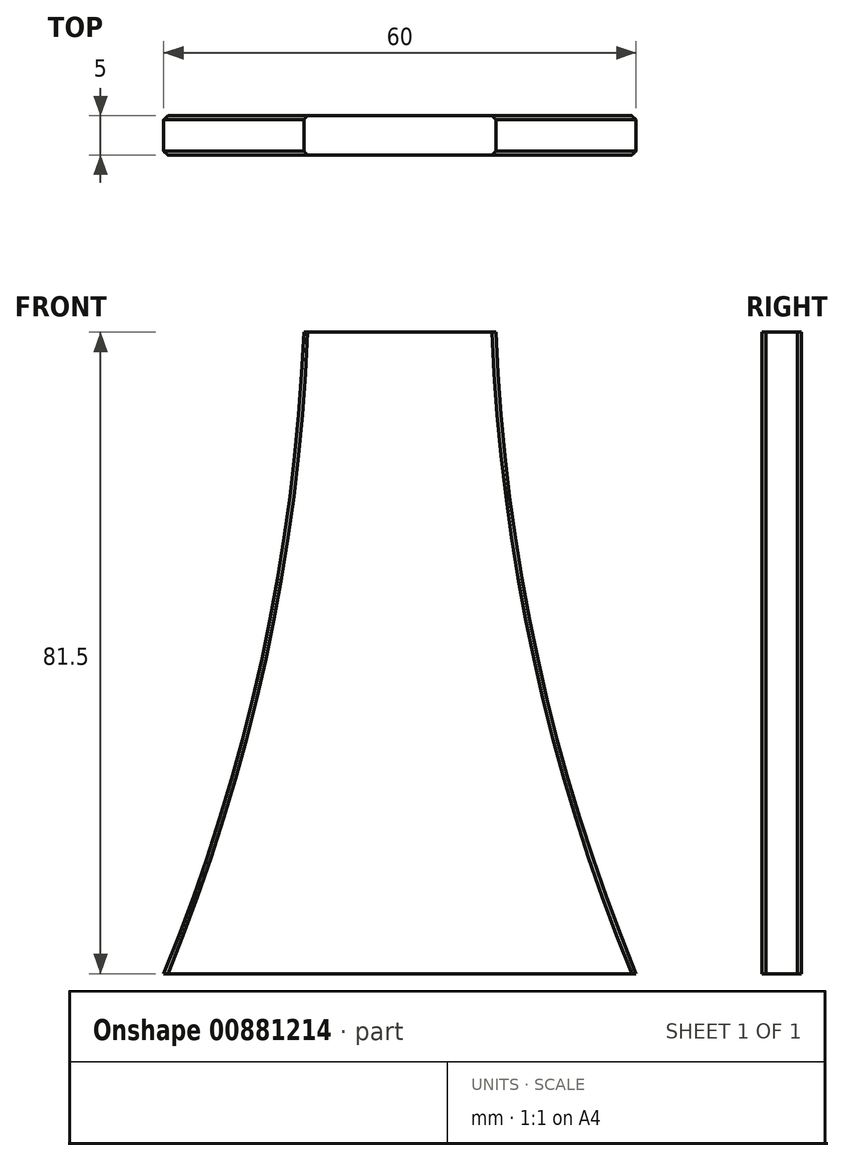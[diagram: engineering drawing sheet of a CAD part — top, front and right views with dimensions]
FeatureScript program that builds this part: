
annotation { "Feature Type Name" : "Feature", "Feature Type Description" : "" }
export const myFeature = defineFeature(function(context is Context, id is Id, definition is map)
    precondition{}
    {
        {
            var Q0;
            Q0=qCreatedBy(makeId("Front.planeOp"),FACE);
            var sketch = newSketch(context, id + "F0", { "sketchPlane" : qUnion([Q0])});
            skLineSegment(sketch, "E0", {"start": v(-12.2, 40.75) * mm, "end": v(12.2, 40.75) * mm});
            skLineSegment(sketch, "E1", {"start": v(-30, -40.75) * mm, "end": v(30, -40.75) * mm});
            skArc(sketch, "E2", {"start": v(-30, -40.75) * mm, "mid": v(-17.53, -0.78) * mm, "end": v(-12.2, 40.75) * mm});
            skArc(sketch, "E3", {"start": v(12.2, 40.75) * mm, "mid": v(17.53, -0.78) * mm, "end": v(30, -40.75) * mm});
            skSolve(sketch);
        }
        {
            var Q0;
            Q0=makeQuery(id+"F0.imprint","IMPRINT",FACE,{"disambiguationData":[TD([[makeQuery(id+"F0.imprint","IMPRINT",EDGE,{"derivedFrom":sQuery(id+"F0.wireOp",EDGE,"E0")}),-1.0]])]});
            extrude(context, id + "F1", {"entities" : qUnion([Q0]), "depth" : 5 * mm, "offsetDistance" : 25 * mm});
        }
        {
            var Q0;
            Q0=makeQuery(id+"F1.opExtrude","CAP_EDGE",EDGE,{"disambiguationData":[OSD([sQuery(id+"F0.wireOp",EDGE,"E2")])],"isStart":true});
            var Q1;
            Q1=makeQuery(id+"F1.opExtrude","CAP_EDGE",EDGE,{"disambiguationData":[OSD([sQuery(id+"F0.wireOp",EDGE,"E2")])],"isStart":false});
            var Q2;
            Q2=makeQuery(id+"F1.opExtrude","CAP_EDGE",EDGE,{"disambiguationData":[OSD([sQuery(id+"F0.wireOp",EDGE,"E3")])],"isStart":false});
            var Q3;
            Q3=makeQuery(id+"F1.opExtrude","CAP_EDGE",EDGE,{"disambiguationData":[OSD([sQuery(id+"F0.wireOp",EDGE,"E3")])],"isStart":true});
            chamfer(context, id + "F2", {"entities" : qUnion([Q0, Q1, Q2, Q3]), "width" : 0.5 * mm, "tangentPropagation" : true});
        }
    });
